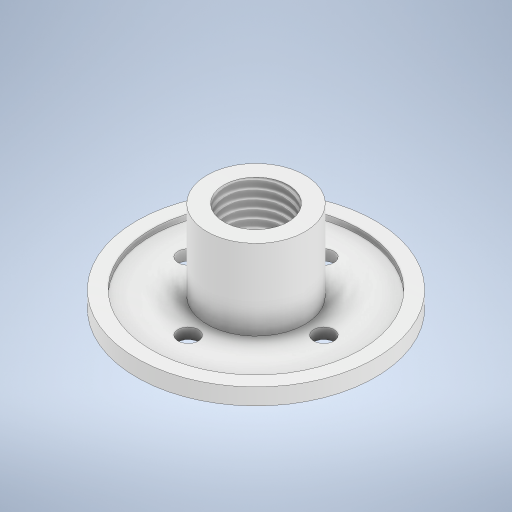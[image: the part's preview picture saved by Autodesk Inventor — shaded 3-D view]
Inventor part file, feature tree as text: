
AUTODESK INVENTOR PART (.ipt)
format: ipt  version: 2024 (Build 280153000, 153)  size: 358,400 bytes
history: native  units: mm
features: extrude x5, other x1, thread x1
ambient origin geometry x8: Origin, YZ Plane, XZ Plane, XY Plane, X Axis, Y Axis, Z Axis, Center Point
bodies: Body1 (feature_tree)
feature tree (7):
  other  "Sólido1"
  extrude  "Extrusión1"  Depth=70.33mm
  extrude  "Extrusión2"  Depth=26.85mm TaperAngle=0.0deg
  thread  "Rosca1"  [1 undecoded]
  extrude  "Extrusión3"  Depth=21.97mm TaperAngle=0.0deg
  extrude  "Extrusión4"  Depth=61.67mm
  extrude  "Extrusión5"  Depth=1.67mm TaperAngle=0.0deg
note: 1 required parameter value undecoded (feature->parameter linkage not recoverable at this tier; creation-order binding heuristic only, values carry confidence <= 0.55)
